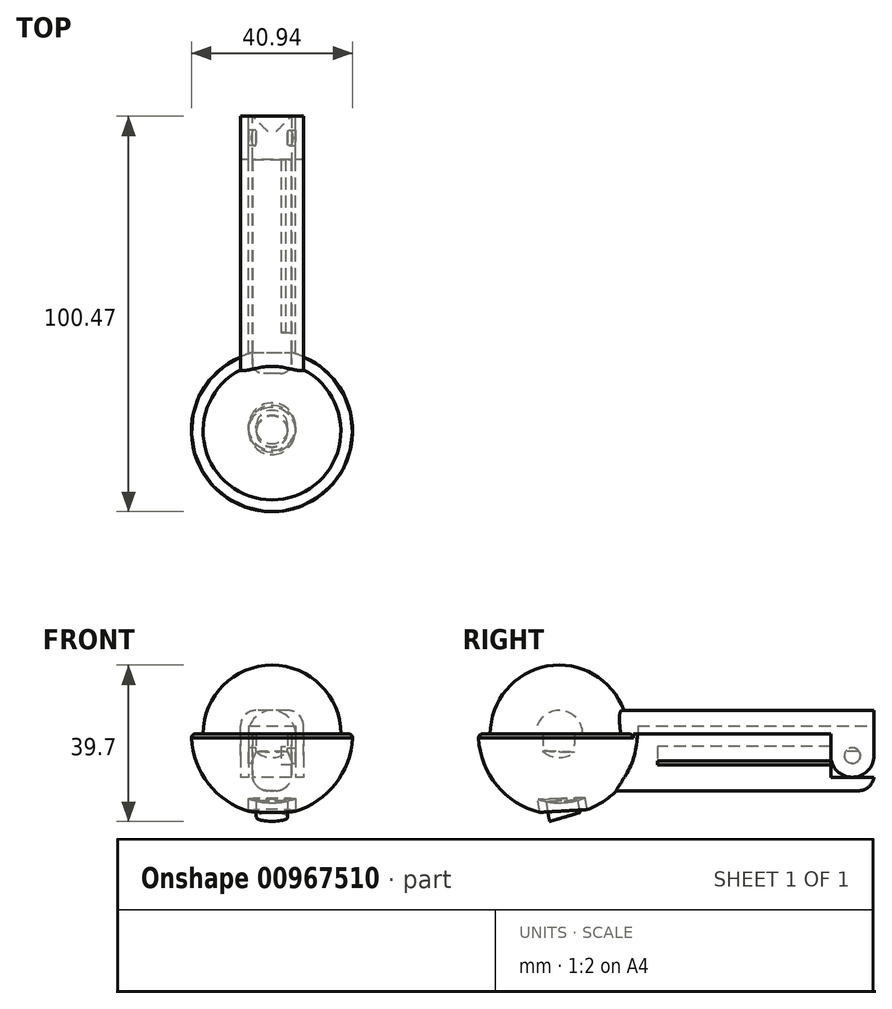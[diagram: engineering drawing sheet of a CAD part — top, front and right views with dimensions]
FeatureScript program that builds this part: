
annotation { "Feature Type Name" : "Feature", "Feature Type Description" : "" }
export const myFeature = defineFeature(function(context is Context, id is Id, definition is map)
    precondition{}
    {
        {
            var Q0;
            Q0=qCreatedBy(makeId("Top.planeOp"),FACE);
            var sketch = newSketch(context, id + "F0", { "sketchPlane" : qUnion([Q0])});
            skArc(sketch, "E0", {"start": v(0, -17.5) * mm, "mid": v(17.5, 0) * mm, "end": v(0, 17.5) * mm});
            skArc(sketch, "E1", {"start": v(0, -20.5) * mm, "mid": v(20.5, 0) * mm, "end": v(0, 20.5) * mm});
            skLineSegment(sketch, "E2", {"start": v(0, 0) * mm, "end": v(0, 38.1) * mm, "construction": true});
            skLineSegment(sketch, "E3", {"start": v(0, 20.5) * mm, "end": v(0, -20.5) * mm});
            skCircle(sketch, "E4", {"center": v(0, 0) * mm, "radius": 6 * mm});
            skCircle(sketch, "E5", {"center": v(0, 0) * mm, "radius": 4 * mm});
            skSolve(sketch);
        }
        {
            var Q0;
            {var subQ0=sQuery(id+"F0.wireOp",EDGE,"E0");Q0=makeQuery(id+"F0.imprint","IMPRINT",FACE,{"disambiguationData":[TD([[makeQuery(id+"F0.imprint","IMPRINT",EDGE,{"derivedFrom":subQ0}),-1.0]])]});}
            var Q1;
            Q1=sQuery(id+"F0.wireOp",EDGE,"E2");
            revolve(context, id + "F1", {"surfaceOperationType" : NewSurfaceOperationType.NEW, "entities" : qUnion([Q0]), "axis" : qUnion([Q1]), "revolveType" : RevolveType.ONE_DIRECTION, "angle" : 180 * degree});
        }
        {
            var Q0;
            Q0=qCreatedBy(makeId("Right.planeOp"),FACE);
            var sketch = newSketch(context, id + "F2", { "sketchPlane" : qUnion([Q0])});
            skLineSegment(sketch, "E6.bottom", {"start": v(0, 0) * mm, "end": v(80, 0) * mm});
            skLineSegment(sketch, "E6.top", {"start": v(0, 6) * mm, "end": v(80, 6) * mm});
            skLineSegment(sketch, "E6.right", {"start": v(80, 0) * mm, "end": v(80, 6) * mm});
            skLineSegment(sketch, "E7.bottom", {"start": v(80, 0) * mm, "end": v(20.5, 0) * mm});
            skLineSegment(sketch, "E7.top", {"start": v(80, -14.43) * mm, "end": v(14.57, -14.43) * mm});
            skLineSegment(sketch, "E7.left", {"start": v(80, 0) * mm, "end": v(80, -14.43) * mm});
            skLineSegment(sketch, "E7.right", {"start": v(14.57, -14.42) * mm, "end": v(14.57, -14.43) * mm});
            skLineSegment(sketch, "E8.bottom", {"start": v(80, 0) * mm, "end": v(69, 0) * mm});
            skLineSegment(sketch, "E8.top", {"start": v(80, -11) * mm, "end": v(69, -11) * mm});
            skLineSegment(sketch, "E8.left", {"start": v(80, 0) * mm, "end": v(80, -11) * mm});
            skLineSegment(sketch, "E8.right", {"start": v(69, 0) * mm, "end": v(69, -11) * mm});
            skCircle(sketch, "E9", {"center": v(74.5, -5.5) * mm, "radius": 2.5 * mm});
            skPoint(sketch, "E9.centerSnap0", {"position": v(80, -5.5) * mm});
            skPoint(sketch, "E9.centerSnap1", {"position": v(74.5, 0) * mm});
            skArc(sketch, "E10", {"start": v(-20.5, 0) * mm, "mid": v(0, -20.5) * mm, "end": v(20.5, 0) * mm});
            skLineSegment(sketch, "E11.bottom", {"start": v(0, 0) * mm, "end": v(-9.53, 0) * mm});
            skLineSegment(sketch, "E11.top", {"start": v(0, 6) * mm, "end": v(-9.53, 6) * mm});
            skLineSegment(sketch, "E11.right", {"start": v(-9.53, 0) * mm, "end": v(-9.53, 6) * mm});
            skPoint(sketch, "E12", {"position": v(1.44, -21.08) * mm});
            skArc(sketch, "E13", {"start": v(0, 0) * mm, "mid": v(-0.03, -10.6) * mm, "end": v(1.44, -21.08) * mm});
            skLineSegment(sketch, "E14", {"start": v(14.57, -14.42) * mm, "end": v(14.57, 0) * mm});
            skArc(sketch, "E15", {"start": v(74.5, -11) * mm, "mid": v(80, -5.5) * mm, "end": v(74.5, 0) * mm});
            skArc(sketch, "E16", {"start": v(74.5, -11) * mm, "mid": v(70.61, -9.39) * mm, "end": v(69, -5.5) * mm});
            skSolve(sketch);
        }
        {
            var Q0;
            {var subQ0=sQuery(id+"F0.wireOp",EDGE,"E4");var subQ1=sQuery(id+"F0.wireOp",EDGE,"E3");var subQ2=makeQuery(id+"F0.imprint","INTERSECT",VERTEX,{"disambiguationData":[OD(0.0)],"derivedFrom":[subQ1,subQ0]});Q0=makeQuery(id+"F0.imprint","IMPRINT",FACE,{"disambiguationData":[TD([[makeQuery(id+"F0.imprint","IMPRINT",EDGE,{"disambiguationData":[TD([[subQ2,-1.0]])],"derivedFrom":subQ1}),1.0]])]});}
            var Q1;
            {var subQ0=sQuery(id+"F0.wireOp",EDGE,"E4");var subQ1=sQuery(id+"F0.wireOp",EDGE,"E3");var subQ2=makeQuery(id+"F0.imprint","INTERSECT",VERTEX,{"disambiguationData":[OD(0.0)],"derivedFrom":[subQ1,subQ0]});Q1=makeQuery(id+"F0.imprint","IMPRINT",FACE,{"disambiguationData":[TD([[makeQuery(id+"F0.imprint","IMPRINT",EDGE,{"disambiguationData":[TD([[subQ2,-1.0]])],"derivedFrom":subQ1}),-1.0]])]});}
            var Q2;
            {var subQ0=sQuery(id+"F0.wireOp",EDGE,"E5");var subQ1=sQuery(id+"F0.wireOp",EDGE,"E3");var subQ2=makeQuery(id+"F0.imprint","INTERSECT",VERTEX,{"disambiguationData":[OD(0.0)],"derivedFrom":[subQ1,subQ0]});Q2=makeQuery(id+"F0.imprint","IMPRINT",FACE,{"disambiguationData":[TD([[makeQuery(id+"F0.imprint","IMPRINT",EDGE,{"disambiguationData":[TD([[subQ2,-1.0]])],"derivedFrom":subQ1}),-1.0]])]});}
            var Q3;
            {var subQ0=sQuery(id+"F0.wireOp",EDGE,"E5");var subQ1=sQuery(id+"F0.wireOp",EDGE,"E3");var subQ2=makeQuery(id+"F0.imprint","INTERSECT",VERTEX,{"disambiguationData":[OD(0.0)],"derivedFrom":[subQ1,subQ0]});Q3=makeQuery(id+"F0.imprint","IMPRINT",FACE,{"disambiguationData":[TD([[makeQuery(id+"F0.imprint","IMPRINT",EDGE,{"disambiguationData":[TD([[subQ2,-1.0]])],"derivedFrom":subQ1}),1.0]])]});}
            var Q4;
            Q4=sQuery(id+"F2.wireOp",EDGE,"E13");
            sweep(context, id + "F3", {"operationType" : NewBodyOperationType.REMOVE, "profiles" : qUnion([Q0, Q1, Q2, Q3]), "path" : qUnion([Q4])});
        }
        {
            var Q0;
            {var subQ6=sQuery(id+"F2.wireOp",EDGE,"E7.top");Q0=makeQuery(id+"F2.imprint","IMPRINT",FACE,{"disambiguationData":[TD([[makeQuery(id+"F2.imprint","IMPRINT",EDGE,{"derivedFrom":subQ6}),-1.0]])]});}
            var Q1;
            {var subQ3=sQuery(id+"F2.wireOp",EDGE,"E14");Q1=makeQuery(id+"F2.imprint","IMPRINT",FACE,{"disambiguationData":[TD([[makeQuery(id+"F2.imprint","IMPRINT",EDGE,{"derivedFrom":subQ3}),-1.0]])]});}
            var Q2;
            {var subQ0=sQuery(id+"F2.wireOp",EDGE,"E16");Q2=makeQuery(id+"F2.imprint","IMPRINT",FACE,{"disambiguationData":[TD([[makeQuery(id+"F2.imprint","IMPRINT",EDGE,{"derivedFrom":subQ0}),1.0]])]});}
            var Q3;
            {var subQ0=sQuery(id+"F2.wireOp",EDGE,"E8.top");var subQ1=sQuery(id+"F2.wireOp",EDGE,"E7.left");var subQ2=makeQuery(id+"F2.imprint","INTERSECT",VERTEX,{"derivedFrom":[subQ1,subQ0]});Q3=makeQuery(id+"F2.imprint","IMPRINT",FACE,{"disambiguationData":[TD([[makeQuery(id+"F2.imprint","IMPRINT",EDGE,{"disambiguationData":[TD([[subQ2,1.0]])],"derivedFrom":subQ1}),-1.0]])]});}
            var Q4;
            Q4=makeQuery(id+"F2.imprint","IMPRINT",FACE,{"disambiguationData":[TD([[makeQuery(id+"F2.imprint","IMPRINT",EDGE,{"derivedFrom":sQuery(id+"F2.wireOp",EDGE,"E9")}),-1.0]])]});
            extrude(context, id + "F4", {"entities" : qUnion([Q0, Q1, Q2, Q3, Q4]), "operationType" : NewBodyOperationType.ADD, "endBound" : BoundingType.SYMMETRIC, "depth" : 10 * mm, "offsetDistance" : 25 * mm});
        }
        {
            var Q0;
            Q0=makeQuery(id+"F2.imprint","IMPRINT",FACE,{"disambiguationData":[TD([[makeQuery(id+"F2.imprint","IMPRINT",EDGE,{"derivedFrom":sQuery(id+"F2.wireOp",EDGE,"E6.top")}),-1.0]])]});
            var Q1;
            {var subQ0=sQuery(id+"F2.wireOp",EDGE,"E15");var subQ1=sQuery(id+"F2.wireOp",EDGE,"E6.bottom");var subQ2=makeQuery(id+"F2.imprint","INTERSECT",VERTEX,{"derivedFrom":[subQ1,subQ0]});Q1=makeQuery(id+"F2.imprint","IMPRINT",FACE,{"disambiguationData":[TD([[makeQuery(id+"F2.imprint","IMPRINT",EDGE,{"disambiguationData":[TD([[subQ2,1.0]])],"derivedFrom":subQ0}),-1.0]])]});}
            var Q2;
            Q2=makeQuery(id+"F2.imprint","IMPRINT",FACE,{"disambiguationData":[TD([[makeQuery(id+"F2.imprint","IMPRINT",EDGE,{"derivedFrom":sQuery(id+"F2.wireOp",EDGE,"E9")}),-1.0]])]});
            var Q3;
            Q3=makeQuery(id+"F2.imprint","IMPRINT",FACE,{"disambiguationData":[TD([[makeQuery(id+"F2.imprint","IMPRINT",EDGE,{"derivedFrom":sQuery(id+"F2.wireOp",EDGE,"E9")}),1.0]])]});
            extrude(context, id + "F5", {"entities" : qUnion([Q0, Q1, Q2, Q3]), "endBound" : BoundingType.SYMMETRIC, "depth" : 16 * mm, "offsetDistance" : 25 * mm});
        }
        {
            var Q0;
            {var subQ0=sQuery(id+"F0.wireOp",EDGE,"E5");var subQ1=sQuery(id+"F0.wireOp",EDGE,"E3");var subQ2=makeQuery(id+"F0.imprint","INTERSECT",VERTEX,{"disambiguationData":[OD(0.0)],"derivedFrom":[subQ1,subQ0]});Q0=makeQuery(id+"F0.imprint","IMPRINT",FACE,{"disambiguationData":[TD([[makeQuery(id+"F0.imprint","IMPRINT",EDGE,{"disambiguationData":[TD([[subQ2,-1.0]])],"derivedFrom":subQ1}),-1.0]])]});}
            var Q1;
            {var subQ0=sQuery(id+"F0.wireOp",EDGE,"E5");var subQ1=sQuery(id+"F0.wireOp",EDGE,"E3");var subQ2=makeQuery(id+"F0.imprint","INTERSECT",VERTEX,{"disambiguationData":[OD(0.0)],"derivedFrom":[subQ1,subQ0]});Q1=makeQuery(id+"F0.imprint","IMPRINT",FACE,{"disambiguationData":[TD([[makeQuery(id+"F0.imprint","IMPRINT",EDGE,{"disambiguationData":[TD([[subQ2,-1.0]])],"derivedFrom":subQ1}),1.0]])]});}
            var Q2;
            Q2=sQuery(id+"F2.wireOp",EDGE,"E13");
            sweep(context, id + "F6", {"operationType" : NewBodyOperationType.ADD, "profiles" : qUnion([Q0, Q1]), "path" : qUnion([Q2])});
        }
        {
            var Q0;
            {var subQ0=sQuery(id+"F2.wireOp",EDGE,"E15");var subQ1=sQuery(id+"F2.wireOp",EDGE,"E6.bottom");var subQ2=makeQuery(id+"F2.imprint","INTERSECT",VERTEX,{"derivedFrom":[subQ1,subQ0]});Q0=makeQuery(id+"F2.imprint","IMPRINT",FACE,{"disambiguationData":[TD([[makeQuery(id+"F2.imprint","IMPRINT",EDGE,{"disambiguationData":[TD([[subQ2,1.0]])],"derivedFrom":subQ0}),-1.0]])]});}
            var Q1;
            {var subQ0=sQuery(id+"F2.wireOp",EDGE,"E8.top");var subQ1=sQuery(id+"F2.wireOp",EDGE,"E7.left");var subQ2=makeQuery(id+"F2.imprint","INTERSECT",VERTEX,{"derivedFrom":[subQ1,subQ0]});Q1=makeQuery(id+"F2.imprint","IMPRINT",FACE,{"disambiguationData":[TD([[makeQuery(id+"F2.imprint","IMPRINT",EDGE,{"disambiguationData":[TD([[subQ2,1.0]])],"derivedFrom":subQ1}),-1.0]])]});}
            var Q2;
            Q2=makeQuery(id+"F2.imprint","IMPRINT",FACE,{"disambiguationData":[TD([[makeQuery(id+"F2.imprint","IMPRINT",EDGE,{"derivedFrom":sQuery(id+"F2.wireOp",EDGE,"E9")}),-1.0]])]});
            var Q3;
            {var subQ0=sQuery(id+"F2.wireOp",EDGE,"E16");Q3=makeQuery(id+"F2.imprint","IMPRINT",FACE,{"disambiguationData":[TD([[makeQuery(id+"F2.imprint","IMPRINT",EDGE,{"derivedFrom":subQ0}),1.0]])]});}
            var Q4;
            Q4=makeQuery(id+"F2.imprint","IMPRINT",FACE,{"disambiguationData":[TD([[makeQuery(id+"F2.imprint","IMPRINT",EDGE,{"derivedFrom":sQuery(id+"F2.wireOp",EDGE,"E9")}),1.0]])]});
            extrude(context, id + "F7", {"entities" : qUnion([Q0, Q1, Q2, Q3, Q4]), "operationType" : NewBodyOperationType.REMOVE, "endBound" : BoundingType.SYMMETRIC, "oppositeDirection" : true, "depth" : 12 * mm, "offsetDistance" : 25 * mm});
        }
        {
            var Q0;
            Q0=makeQuery(id+"F7.boolean.opBoolean","COPY",FACE,{"derivedFrom":makeQuery(id+"F7.opExtrude","CAP_FACE",FACE,{"disambiguationData":[OSD([sQuery(id+"F2.wireOp",EDGE,"E6.bottom"),sQuery(id+"F2.wireOp",EDGE,"E7.left"),sQuery(id+"F2.wireOp",EDGE,"E8.top"),sQuery(id+"F2.wireOp",EDGE,"E8.right")])],"isStart":true})});
            var sketch = newSketch(context, id + "F8", { "sketchPlane" : qUnion([Q0])});
            skPoint(sketch, "E17.0", {"position": v(-74.5, -5.5) * mm});
            skCircle(sketch, "E18.0", {"center": v(-74.5, -5.5) * mm, "radius": 2.5 * mm});
            skCircle(sketch, "E19", {"center": v(-74.5, -5.5) * mm, "radius": 2 * mm});
            skSolve(sketch);
        }
        {
            var Q0;
            Q0=makeQuery(id+"F8.imprint","IMPRINT",FACE,{"disambiguationData":[TD([[makeQuery(id+"F8.imprint","IMPRINT",EDGE,{"derivedFrom":sQuery(id+"F8.wireOp",EDGE,"E19")}),1.0]])]});
            extrude(context, id + "F9", {"entities" : qUnion([Q0]), "operationType" : NewBodyOperationType.ADD, "depth" : 2 * mm, "offsetDistance" : 25 * mm});
        }
        {
            var Q0;
            Q0=qCreatedBy(makeId("Front.planeOp"),FACE);
            var sketch = newSketch(context, id + "F10", { "sketchPlane" : qUnion([Q0])});
            skLineSegment(sketch, "E20", {"start": v(3.47, -3.21) * mm, "end": v(2.3, -3.21) * mm});
            skLineSegment(sketch, "E21", {"start": v(3.47, -3.21) * mm, "end": v(5.43, -7.85) * mm});
            skLineSegment(sketch, "E22", {"start": v(2.3, -7.85) * mm, "end": v(5.43, -7.85) * mm});
            skLineSegment(sketch, "E23", {"start": v(2.3, -7.85) * mm, "end": v(2.3, -3.21) * mm});
            skSolve(sketch);
        }
        {
            var Q0;
            Q0=makeQuery(id+"F10.imprint","IMPRINT",FACE,{"disambiguationData":[TD([[makeQuery(id+"F10.imprint","IMPRINT",EDGE,{"derivedFrom":sQuery(id+"F10.wireOp",EDGE,"E20")}),1.0]])]});
            extrude(context, id + "F11", {"entities" : qUnion([Q0]), "operationType" : NewBodyOperationType.REMOVE, "endBound" : BoundingType.THROUGH_ALL, "oppositeDirection" : true, "depth" : 25 * mm, "offsetDistance" : 25 * mm, "hasSecondDirection" : true, "secondDirectionOppositeDirection" : true, "secondDirectionDepth" : 25 * mm});
        }
        {
            var Q0;
            Q0=makeQuery(id+"F5.opExtrude","SWEPT_BODY",BODY,{"disambiguationData":[OSD([sQuery(id+"F2.wireOp",EDGE,"E6.bottom"),sQuery(id+"F2.wireOp",EDGE,"E6.top"),sQuery(id+"F2.wireOp",EDGE,"E6.right"),sQuery(id+"F2.wireOp",EDGE,"E7.left"),sQuery(id+"F2.wireOp",EDGE,"E8.right"),sQuery(id+"F2.wireOp",EDGE,"E11.bottom"),sQuery(id+"F2.wireOp",EDGE,"E11.top"),sQuery(id+"F2.wireOp",EDGE,"E11.right"),sQuery(id+"F2.wireOp",EDGE,"E15"),sQuery(id+"F2.wireOp",EDGE,"E16")])]});
            var Q1;
            Q1=qCreatedBy(makeId("Right.planeOp"),FACE);
            mirror(context, id + "F12", {"operationType" : NewBodyOperationType.ADD, "entities" : qUnion([Q0]), "mirrorPlane" : qUnion([Q1])});
        }
        {
            var Q0;
            {var subQ0=sQuery(id+"F0.wireOp",EDGE,"E0");Q0=makeQuery(id+"F0.imprint","IMPRINT",FACE,{"disambiguationData":[TD([[makeQuery(id+"F0.imprint","IMPRINT",EDGE,{"derivedFrom":subQ0}),1.0]])]});}
            var Q1;
            Q1=sQuery(id+"F2.wireOp",EDGE,"E7.bottom");
            revolve(context, id + "F13", {"operationType" : NewBodyOperationType.REMOVE, "surfaceOperationType" : NewSurfaceOperationType.NEW, "entities" : qUnion([Q0]), "axis" : qUnion([Q1]), "revolveType" : RevolveType.FULL, "oppositeDirection" : true});
        }
        {
            var Q0;
            Q0=makeQuery(id+"F5.opExtrude","CAP_EDGE",EDGE,{"disambiguationData":[OSD([sQuery(id+"F2.wireOp",EDGE,"E11.right")])],"isStart":true});
            var Q1;
            Q1=makeQuery(id+"F5.opExtrude","CAP_EDGE",EDGE,{"disambiguationData":[OSD([sQuery(id+"F2.wireOp",EDGE,"E11.right")])],"isStart":false});
            var Q2;
            Q2=makeQuery(id+"F4.opExtrude","CAP_EDGE",EDGE,{"disambiguationData":[OSD([sQuery(id+"F2.wireOp",EDGE,"E7.top")])],"isStart":true});
            var Q3;
            Q3=makeQuery(id+"F4.opExtrude","CAP_EDGE",EDGE,{"disambiguationData":[OSD([sQuery(id+"F2.wireOp",EDGE,"E7.top")])],"isStart":false});
            var Q4;
            {var subQ0=sQuery(id+"F2.wireOp",EDGE,"E6.bottom");var subQ1=sQuery(id+"F0.wireOp",EDGE,"E1");Q4=makeQuery(id+"F4.boolean.opBoolean","SPLIT",EDGE,{"disambiguationData":[TD([makeQuery(id+"F1.opRevolve","SWEPT_FACE",FACE,{"disambiguationData":[OSD([subQ1])]})])],"derivedFrom":makeQuery(id+"F4.opExtrude","CAP_EDGE",EDGE,{"disambiguationData":[OSD([subQ0])],"isStart":true})});}
            var Q5;
            {var subQ0=sQuery(id+"F2.wireOp",EDGE,"E6.bottom");var subQ2=sQuery(id+"F0.wireOp",EDGE,"E1");Q5=makeQuery(id+"F4.boolean.opBoolean","SPLIT",EDGE,{"disambiguationData":[TD([makeQuery(id+"F1.opRevolve","SWEPT_FACE",FACE,{"disambiguationData":[OSD([subQ2])]})])],"derivedFrom":makeQuery(id+"F4.opExtrude","CAP_EDGE",EDGE,{"disambiguationData":[OSD([subQ0])],"isStart":false})});}
            var Q6;
            Q6=makeQuery(id+"F5.opExtrude","CAP_EDGE",EDGE,{"disambiguationData":[OSD([sQuery(id+"F2.wireOp",EDGE,"E6.top"),sQuery(id+"F2.wireOp",EDGE,"E11.top")])],"isStart":true});
            var Q7;
            Q7=makeQuery(id+"F5.opExtrude","CAP_EDGE",EDGE,{"disambiguationData":[OSD([sQuery(id+"F2.wireOp",EDGE,"E6.top"),sQuery(id+"F2.wireOp",EDGE,"E11.top")])],"isStart":false});
            var Q8;
            Q8=makeQuery(id+"F4.opExtrude","SWEPT_EDGE",EDGE,{"disambiguationData":[OSD([sQuery(id+"F2.wireOp",EDGE,"E7.top"),sQuery(id+"F2.wireOp",EDGE,"E7.left")])]});
            var Q9;
            Q9=makeQuery(id+"F5.opExtrude","SWEPT_EDGE",EDGE,{"disambiguationData":[OSD([sQuery(id+"F2.wireOp",EDGE,"E11.top"),sQuery(id+"F2.wireOp",EDGE,"E11.right")])]});
            fillet(context, id + "F14", {"entities" : qUnion([Q0, Q1, Q2, Q3, Q4, Q5, Q6, Q7, Q8, Q9]), "radius" : 4 * mm, "tangentPropagation" : true, "allowEdgeOverflow" : false});
        }
        {
            var Q0;
            {var subQ0=sQuery(id+"F0.wireOp",EDGE,"E0");Q0=makeQuery(id+"F13.boolean.opBoolean","INTERSECT",EDGE,{"derivedFrom":[makeQuery(id+"F4.boolean.opBoolean","MERGE",FACE,{"derivedFrom":[makeQuery(id+"F1.opRevolve","CAP_FACE",FACE,{"disambiguationData":[OSD([subQ0,sQuery(id+"F0.wireOp",EDGE,"E1"),sQuery(id+"F0.wireOp",EDGE,"E3")])],"isStart":true}),makeQuery(id+"F4.opExtrude","SWEPT_FACE",FACE,{"disambiguationData":[OSD([sQuery(id+"F2.wireOp",EDGE,"E6.bottom")])]})]}),makeQuery(id+"F13.opRevolve","SWEPT_FACE",FACE,{"disambiguationData":[OSD([subQ0])]})]});}
            var Q1;
            Q1=makeQuery(id+"F1.opRevolve","CAP_EDGE",EDGE,{"disambiguationData":[OSD([sQuery(id+"F0.wireOp",EDGE,"E1")])],"isStart":true});
            fillet(context, id + "F15", {"entities" : qUnion([Q0, Q1]), "radius" : 1 * mm, "tangentPropagation" : true, "allowEdgeOverflow" : false});
        }
        {
            var Q0;
            Q0=qCreatedBy(makeId("Front.planeOp"),FACE);
            cPlane(context, id + "F16", {"entities" : qUnion([Q0]), "cplaneType" : CPlaneType.OFFSET, "offset" : 74.5 * mm, "oppositeDirection" : true, "width" : 150 * mm, "height" : 150 * mm});
        }
        {
            var Q0;
            Q0=qCreatedBy(id+"F16.planeOp",FACE);
            var sketch = newSketch(context, id + "F17", { "sketchPlane" : qUnion([Q0])});
            skLineSegment(sketch, "E24", {"start": v(0, -5.63) * mm, "end": v(-52.46, -5.63) * mm, "construction": true});
            skSolve(sketch);
        }
        {
            var Q0;
            Q0=makeQuery(id+"F5.opExtrude","SWEPT_FACE",FACE,{"disambiguationData":[OSD([sQuery(id+"F2.wireOp",EDGE,"E6.right"),sQuery(id+"F2.wireOp",EDGE,"E7.left")])]});
            var sketch = newSketch(context, id + "F18", { "sketchPlane" : qUnion([Q0])});
            skLineSegment(sketch, "E25.0", {"start": v(6, 0) * mm, "end": v(-6, 0) * mm});
            skLineSegment(sketch, "E26", {"start": v(-6, 0) * mm, "end": v(-6, 2) * mm});
            skLineSegment(sketch, "E27", {"start": v(6, 2) * mm, "end": v(6, 0) * mm});
            skLineSegment(sketch, "E28", {"start": v(6, 2) * mm, "end": v(-6, 2) * mm});
            skSolve(sketch);
        }
        {
            var Q0;
            Q0=makeQuery(id+"F18.imprint","IMPRINT",FACE,{"disambiguationData":[TD([[makeQuery(id+"F18.imprint","IMPRINT",EDGE,{"derivedFrom":sQuery(id+"F18.wireOp",EDGE,"E25.0")}),-1.0]])]});
            extrude(context, id + "F19", {"entities" : qUnion([Q0]), "operationType" : NewBodyOperationType.REMOVE, "oppositeDirection" : true, "depth" : 60 * mm, "offsetDistance" : 25 * mm});
        }
    });
